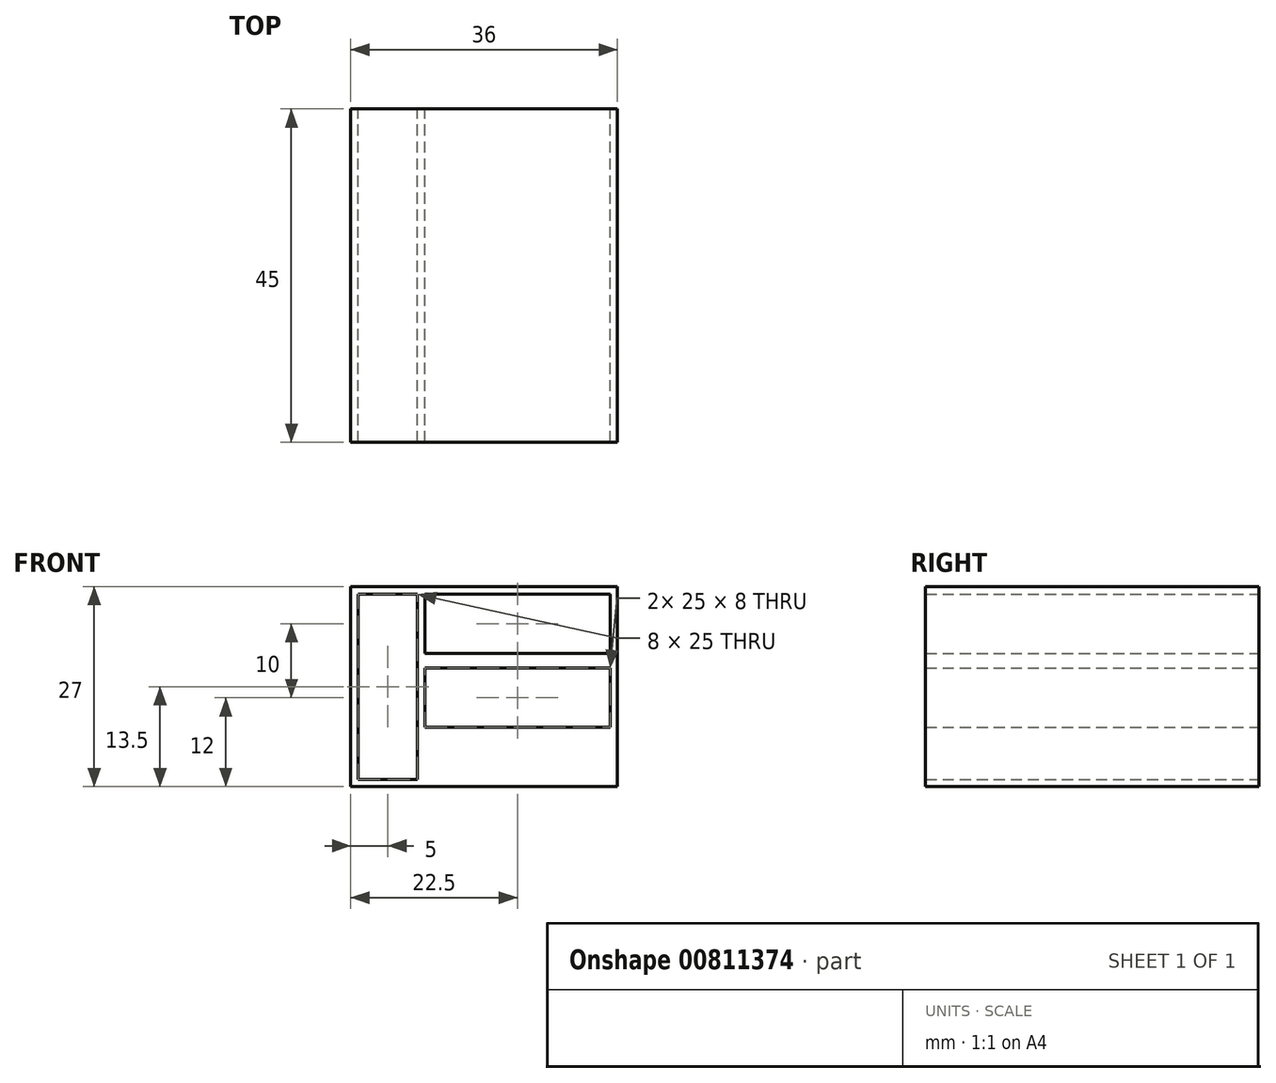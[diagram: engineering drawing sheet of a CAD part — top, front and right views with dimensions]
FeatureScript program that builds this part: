
annotation { "Feature Type Name" : "Feature", "Feature Type Description" : "" }
export const myFeature = defineFeature(function(context is Context, id is Id, definition is map)
    precondition{}
    {
        {
            var Q0;
            Q0=qCreatedBy(makeId("Front.planeOp"),FACE);
            var sketch = newSketch(context, id + "F0", { "sketchPlane" : qUnion([Q0])});
            skLineSegment(sketch, "E0.bottom", {"start": v(-12.5, -4) * mm, "end": v(12.5, -4) * mm});
            skLineSegment(sketch, "E0.top", {"start": v(-12.5, 4) * mm, "end": v(12.5, 4) * mm});
            skLineSegment(sketch, "E0.left", {"start": v(-12.5, -4) * mm, "end": v(-12.5, 4) * mm});
            skLineSegment(sketch, "E0.right", {"start": v(12.5, -4) * mm, "end": v(12.5, 4) * mm});
            skPoint(sketch, "E0.middle", {"position": v(0, 0) * mm});
            skLineSegment(sketch, "E1.0.1.0", {"start": v(-12.5, 14) * mm, "end": v(12.5, 14) * mm});
            skLineSegment(sketch, "E1.0.1.1", {"start": v(-12.5, 6) * mm, "end": v(-12.5, 14) * mm});
            skLineSegment(sketch, "E1.0.1.2", {"start": v(-12.5, 6) * mm, "end": v(12.5, 6) * mm});
            skLineSegment(sketch, "E1.0.1.3", {"start": v(12.5, 6) * mm, "end": v(12.5, 14) * mm});
            skLineSegment(sketch, "E1.direction1", {"start": v(-12.5, 4) * mm, "end": v(12.5, 4) * mm, "construction": true});
            skLineSegment(sketch, "E1.direction2", {"start": v(-12.5, 4) * mm, "end": v(-12.5, 14) * mm, "construction": true});
            skLineSegment(sketch, "E2.bottom", {"start": v(-13.5, 14) * mm, "end": v(-21.5, 14) * mm});
            skLineSegment(sketch, "E2.top", {"start": v(-13.5, -11) * mm, "end": v(-21.5, -11) * mm});
            skLineSegment(sketch, "E2.left", {"start": v(-13.5, 14) * mm, "end": v(-13.5, -11) * mm});
            skLineSegment(sketch, "E2.right", {"start": v(-21.5, 14) * mm, "end": v(-21.5, -11) * mm});
            skLineSegment(sketch, "E3.bottom", {"start": v(-22.5, 15) * mm, "end": v(13.5, 15) * mm});
            skLineSegment(sketch, "E3.top", {"start": v(-22.5, -12) * mm, "end": v(13.5, -12) * mm});
            skLineSegment(sketch, "E3.left", {"start": v(-22.5, 15) * mm, "end": v(-22.5, -12) * mm});
            skLineSegment(sketch, "E3.right", {"start": v(13.5, 15) * mm, "end": v(13.5, -12) * mm});
            skSolve(sketch);
        }
        {
            var Q0;
            Q0=makeQuery(id+"F0.imprint","IMPRINT",FACE,{"disambiguationData":[TD([[makeQuery(id+"F0.imprint","IMPRINT",EDGE,{"derivedFrom":sQuery(id+"F0.wireOp",EDGE,"E0.bottom")}),-1.0]])]});
            extrude(context, id + "F1", {"entities" : qUnion([Q0]), "depth" : 45 * mm, "offsetDistance" : 25 * mm});
        }
    });
